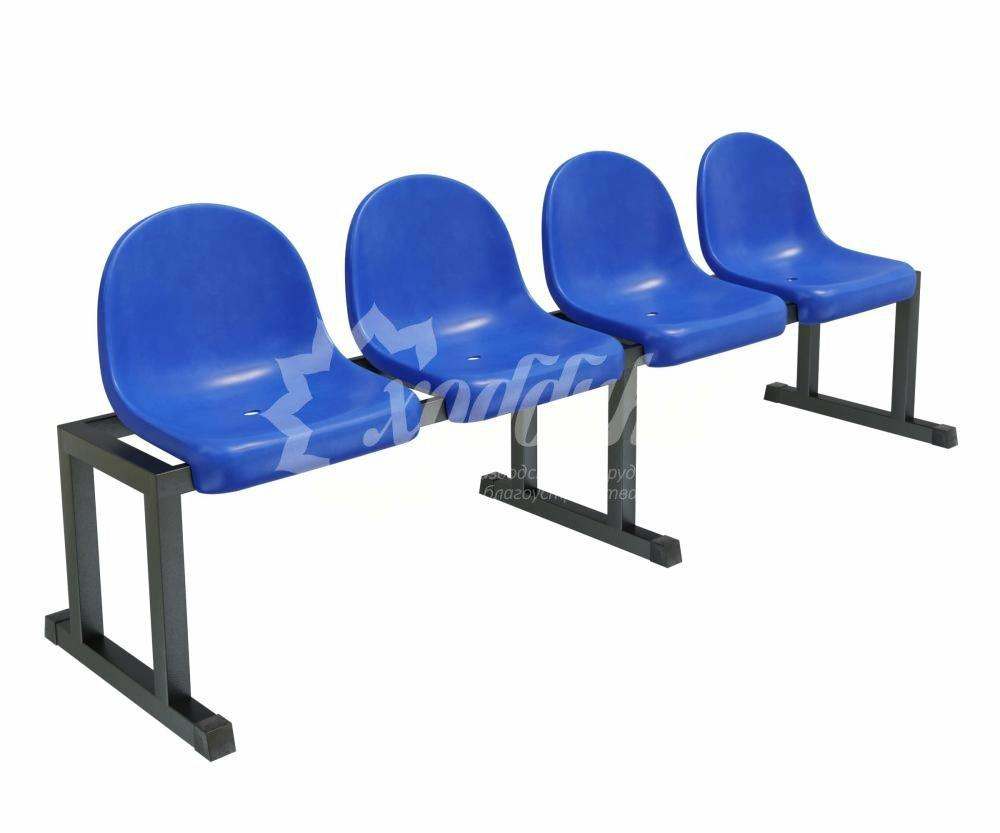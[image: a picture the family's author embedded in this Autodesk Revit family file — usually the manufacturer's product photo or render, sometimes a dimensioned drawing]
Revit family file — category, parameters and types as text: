
# Revit family: 29967 Трибуна однорядная мобильная на 4 места «Сингл-4» Хоббика
name_source: partatom
category: Антураж
revit_build: Autodesk Revit 2018 (Build: 20180423_1000(x64)
units: mm (PartAtom-declared; Revit-internal decimal feet)

## family parameters
Всегда вертикально = Да
Источник визуального образа = Геометрия семейства
На основе рабочей плоскости = Нет
Общий = Нет
При загрузке вырезать с полостями = Нет
Точка расчета площади = Нет

## types (1)
- Трибуна однорядная мобильная на 4 места «Сингл-4»
    URL = https://hobbyka.ru
    Артикул товара = Арт. 29967
    Высота = 700 мм
    Группа модели = Мобильные и стационарные трибуны
    Длина = 2140 мм
    Изготовитель = ООО «Хоббика»
    Изображение типоразмера = Трибуна однорядная мобильная на 4 места «Сингл-4» Арт 29967.jpg
    Материал изделия = Сталь, пластик
    Описание = Трибуна однорядная мобильная на 4 места «Сингл-4»
    Цвет каркаса = Сталь
    Цвет сидений = Красный
    Ширина = 530 мм

## geometry (parser evidence)
native form markers: Sweep x1
no freeform markers — native parametric forms only
